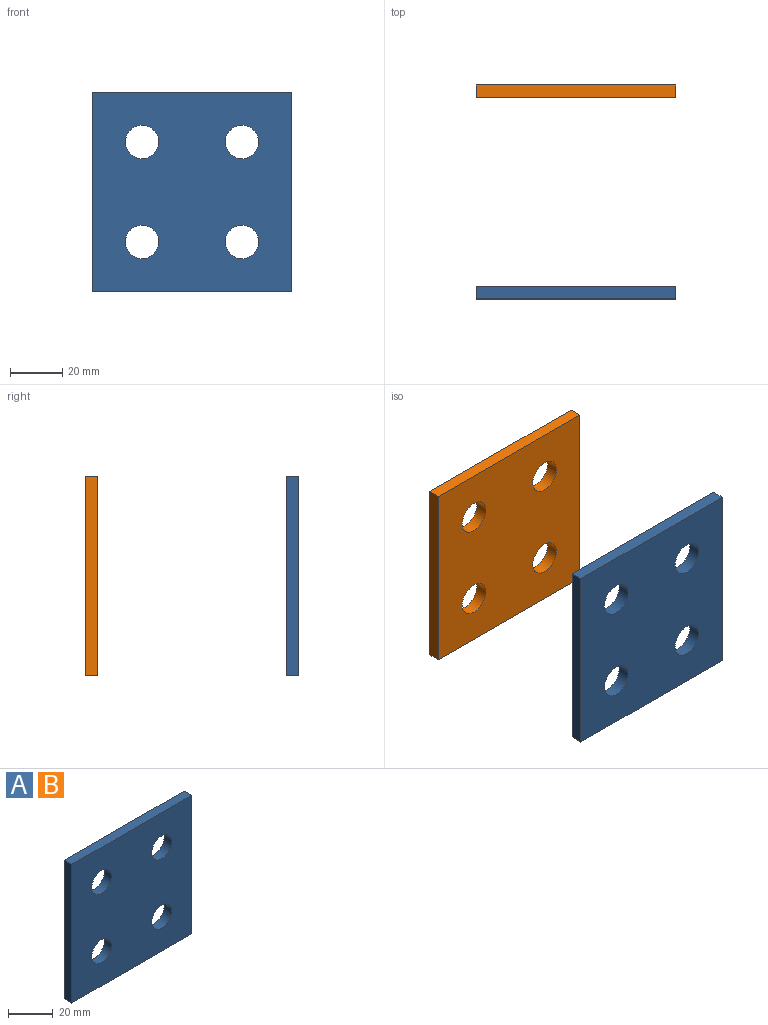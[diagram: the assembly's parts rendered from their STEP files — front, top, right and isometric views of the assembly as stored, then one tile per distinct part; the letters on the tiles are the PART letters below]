
ASSEMBLY  parts=2 mates=1
PART A: 10 faces, bbox 76.2x4.8x76.2 mm
  f0: plane 76.2x4.76mm, normal (0,0,1), area 362.9mm2, adj f1,f7,f8,f9
  f1: plane 76.2x4.76mm, normal (-1,0,0), area 362.9mm2, adj f0,f2,f8,f9
  f2: plane 76.2x4.76mm, normal (0,0,-1), area 362.9mm2, adj f1,f7,f8,f9
  f3: cylinder r=6.35mm len=12.7mm, axis (0,1,0), area 190mm2, adj f8,f9
  f4: cylinder r=6.35mm len=12.7mm, axis (0,1,0), area 190mm2, adj f8,f9
  f5: cylinder r=6.35mm len=12.7mm, axis (0,1,0), area 190mm2, adj f8,f9
  f6: cylinder r=6.35mm len=12.7mm, axis (0,1,0), area 190mm2, adj f8,f9
  f7: plane 76.2x4.76mm, normal (1,0,0), area 362.9mm2, adj f0,f2,f8,f9
  f8: plane 76.2x76.2mm, normal (0,-1,0), area 5299.7mm2, adj f0,f1,f2,f3,f4,f5,f6,f7
  f9: plane 76.2x76.2mm, normal (0,1,0), area 5299.7mm2, adj f0,f1,f2,f3,f4,f5,f6,f7
PART B: same geometry as A
PLACE A t=(11.41,-65.1,3.99)mm
PLACE B t=(11.41,11.63,3.99)mm fixed
MATE slider A.f6 <-> B.f6  axis (0,-1,0) through (30.46,-69.86,23.04)mm
